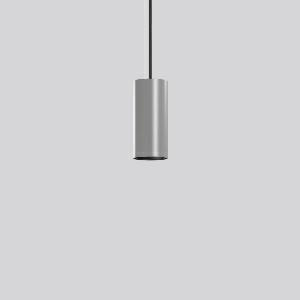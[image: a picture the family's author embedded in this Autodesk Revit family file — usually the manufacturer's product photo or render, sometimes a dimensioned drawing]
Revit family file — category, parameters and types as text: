
# Revit family: deecos_p_mini_911515_004_3_917e
name_source: partatom
category: Lighting Fixtures
units: mm (PartAtom-declared; Revit-internal decimal feet)

## family parameters
Cut with Voids When Loaded = No
Host = Face
Light Source = No
Part Type = Normal
Room Calculation Point = No
Round Connector Dimension = Use Diameter
Shared = No

## types (1)
- DEECOS P mini (1 x LED Modul 935, 2650 lm, 3500)
    Apparent Load = 20 VA
    Approval mark = CE
    CIE Flux Codes = 95 99 100 100 100
    Color Rendering = 92
    Color Temperature = 3500
    Default Elevation = 1800 mm
    Description = Series: DEECOS P mini
Cylindrical pendant luminaire. Housing: die-cast aluminium, powder-coated. Canopy made of powder-coated sheet steel with magnetic attachment. Optical assembly with reflector made of MIRO-Silver with 98% total light reflection for outstanding efficiency - can be changed without tools. Best colour rendering index Ra>90. Transparent pendant cable 5 m, can be shortened, with integrated steel cable. High quality converter without flickering and stroboscopic effect. The following accessories can be mounted without use of tools: interchangeable lenses, honeycomb louvre, clear and frosted diffusers, white interchangeable plastic ring. Decorative recessed suspension set available as accessory.Suitable for accessory Deecos P Tube cylinder extensions 0.5 m, 0.75 m or 1 m. 
Colour: silver
Diameter: 87 mm
Height: 195 mm
Suspension length: 5000 mm
Lamp: LED
Socket: without socket
Colour temperature: 3500K
Colour rendering index (CRI): 92
System power: 20 W
Rated luminous flux: 2650 lm
Luminous efficiency: 133 lm/W
Control gear: Regulated power supply
Protection class: I
Type of protection: IP 20
    Height = 195 mm
    Lamp = 1 x LED Modul 935
    Lamp Light Flux = 2650 lm
    Lamp count = 1
    Length = 87 mm
    Lifetime = 50000 h
    Luminous efficacy = 133 lm/W
    Manufacturer = RZB
    ModVariant = No
    Model = 911515.004.3
    Mounting Place = Ceiling
    Mounting Type = Pendant
    Number of Poles = 1
    OnlyDefault = Yes
    Power Factor = 1
    Product Name = DEECOS P mini
    Product group = Pendant luminaires
    ProductGroupID = 902
    Protection Class = Protection class I
    Protection Degree = IP 20
    RLX_Detail_Level = 1
    RLX_Emergency_Light_Flux = 0 lm
    RLX_Emergency_Type = 0
    RLX_Emergency_Type_DB = No
    RlxData = <blob elided: 55225 chars, md5=252bcd5b>
    Socket = socket
    Standby Power = 0 W
    System Light Flux = 2650 lm
    System Power = 20 W
    Type Comments = Product without accessories
    Type Image = 911476.004.jpg
    URL = http://relux.com
    VarID = ---
    Voltage = 230 V
    Voltage Range = 220-240 V
    Weight = 0.00 kg
    Width = 0 mm  [stored 0 ft]

note: [stored X ft] marks values corroborated as IEEE doubles in the binary element streams (Revit-internal decimal feet)

## geometry (parser evidence)
native form markers: Blend x4, Sweep x13
no freeform markers — native parametric forms only
